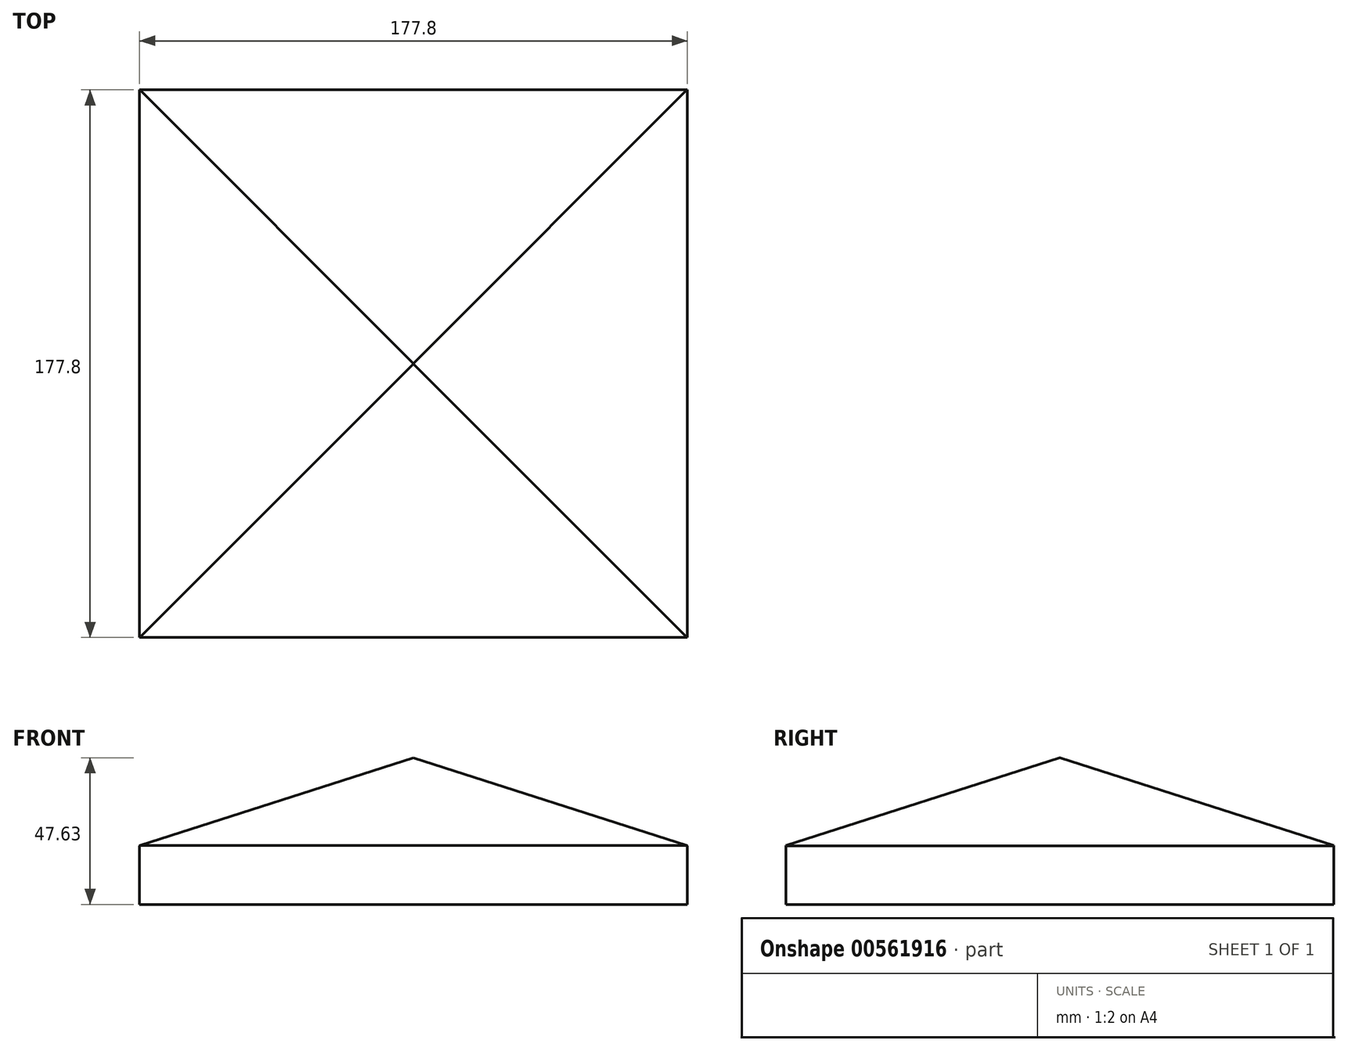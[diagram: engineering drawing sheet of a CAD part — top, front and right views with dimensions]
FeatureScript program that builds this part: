
annotation { "Feature Type Name" : "Feature", "Feature Type Description" : "" }
export const myFeature = defineFeature(function(context is Context, id is Id, definition is map)
    precondition{}
    {
        {
            var Q0;
            Q0=qCreatedBy(makeId("Top.planeOp"),FACE);
            var sketch = newSketch(context, id + "F0", { "sketchPlane" : qUnion([Q0])});
            skLineSegment(sketch, "E0.bottom", {"start": v(0, 0) * mm, "end": v(-177.8, 0) * mm});
            skLineSegment(sketch, "E0.top", {"start": v(0, 177.8) * mm, "end": v(-177.8, 177.8) * mm});
            skLineSegment(sketch, "E0.left", {"start": v(0, 0) * mm, "end": v(0, 177.8) * mm});
            skLineSegment(sketch, "E0.right", {"start": v(-177.8, 0) * mm, "end": v(-177.8, 177.8) * mm});
            skSolve(sketch);
        }
        {
            var Q0;
            Q0 = qSketchRegion(id + "F0", true);
            extrude(context, id + "F1", {"entities" : qUnion([Q0]), "depth" : 47.62 * mm, "offsetDistance" : 25.4 * mm});
        }
        {
            var Q0;
            Q0=makeQuery(id+"F1.opExtrude","SWEPT_FACE",FACE,{"disambiguationData":[OSD([sQuery(id+"F0.wireOp",EDGE,"E0.bottom")])]});
            var sketch = newSketch(context, id + "F2", { "sketchPlane" : qUnion([Q0])});
            skLineSegment(sketch, "E1.0", {"start": v(0, 19.05) * mm, "end": v(-177.8, 19.05) * mm});
            skLineSegment(sketch, "E2.0", {"start": v(-88.9, 47.63) * mm, "end": v(-88.9, 0) * mm});
            skLineSegment(sketch, "E3", {"start": v(-177.8, 19.05) * mm, "end": v(-88.9, 47.63) * mm});
            skLineSegment(sketch, "E4", {"start": v(-88.9, 47.63) * mm, "end": v(0, 19.05) * mm});
            skSolve(sketch);
        }
        {
            var Q0;
            Q0=makeQuery(id+"F1.opExtrude","SWEPT_FACE",FACE,{"disambiguationData":[OSD([sQuery(id+"F0.wireOp",EDGE,"E0.right")])]});
            var sketch = newSketch(context, id + "F3", { "sketchPlane" : qUnion([Q0])});
            skLineSegment(sketch, "E5.0", {"start": v(0, 19.09) * mm, "end": v(-177.8, 19.09) * mm});
            skLineSegment(sketch, "E6.0", {"start": v(-88.9, 47.66) * mm, "end": v(-88.9, 0.04) * mm});
            skLineSegment(sketch, "E7", {"start": v(-177.8, 19.09) * mm, "end": v(-88.9, 47.66) * mm});
            skLineSegment(sketch, "E8", {"start": v(-88.9, 47.66) * mm, "end": v(0, 19.09) * mm});
            skSolve(sketch);
        }
        {
            var Q0;
            {var subQ0=sQuery(id+"F3.wireOp",EDGE,"E7");var subQ1=sQuery(id+"F0.wireOp",EDGE,"E0.right");var subQ4=makeQuery(id+"F1.opExtrude","CAP_EDGE",EDGE,{"disambiguationData":[OSD([subQ1])],"isStart":false});var subQ5=makeQuery(id+"F3.imprint","INTERSECT",VERTEX,{"derivedFrom":[subQ4,subQ0]});Q0=makeQuery(id+"F3.imprint","IMPRINT",FACE,{"disambiguationData":[TD([[makeQuery(id+"F3.imprint","IMPRINT",EDGE,{"disambiguationData":[TD([[subQ5,-1.0]])],"derivedFrom":subQ4}),1.0]])]});}
            var Q1;
            {var subQ0=sQuery(id+"F3.wireOp",EDGE,"E8");var subQ1=sQuery(id+"F0.wireOp",EDGE,"E0.right");var subQ4=makeQuery(id+"F1.opExtrude","CAP_EDGE",EDGE,{"disambiguationData":[OSD([subQ1])],"isStart":false});var subQ5=makeQuery(id+"F3.imprint","INTERSECT",VERTEX,{"derivedFrom":[subQ4,subQ0]});Q1=makeQuery(id+"F3.imprint","IMPRINT",FACE,{"disambiguationData":[TD([[makeQuery(id+"F3.imprint","IMPRINT",EDGE,{"disambiguationData":[TD([[subQ5,1.0]])],"derivedFrom":subQ4}),1.0]])]});}
            extrude(context, id + "F4", {"entities" : qUnion([Q0, Q1]), "operationType" : NewBodyOperationType.REMOVE, "endBound" : BoundingType.THROUGH_ALL, "oppositeDirection" : true, "depth" : 25.4 * mm, "offsetDistance" : 25.4 * mm});
        }
        {
            var Q0;
            {var subQ0=sQuery(id+"F2.wireOp",EDGE,"E3");Q0=makeQuery(id+"F2.imprint","IMPRINT",FACE,{"disambiguationData":[TD([[makeQuery(id+"F2.imprint","IMPRINT",EDGE,{"derivedFrom":subQ0}),1.0]])]});}
            var Q1;
            {var subQ0=sQuery(id+"F2.wireOp",EDGE,"E4");Q1=makeQuery(id+"F2.imprint","IMPRINT",FACE,{"disambiguationData":[TD([[makeQuery(id+"F2.imprint","IMPRINT",EDGE,{"derivedFrom":subQ0}),1.0]])]});}
            extrude(context, id + "F5", {"entities" : qUnion([Q0, Q1]), "operationType" : NewBodyOperationType.REMOVE, "endBound" : BoundingType.THROUGH_ALL, "oppositeDirection" : true, "depth" : 25.4 * mm, "offsetDistance" : 25.4 * mm});
        }
    });
